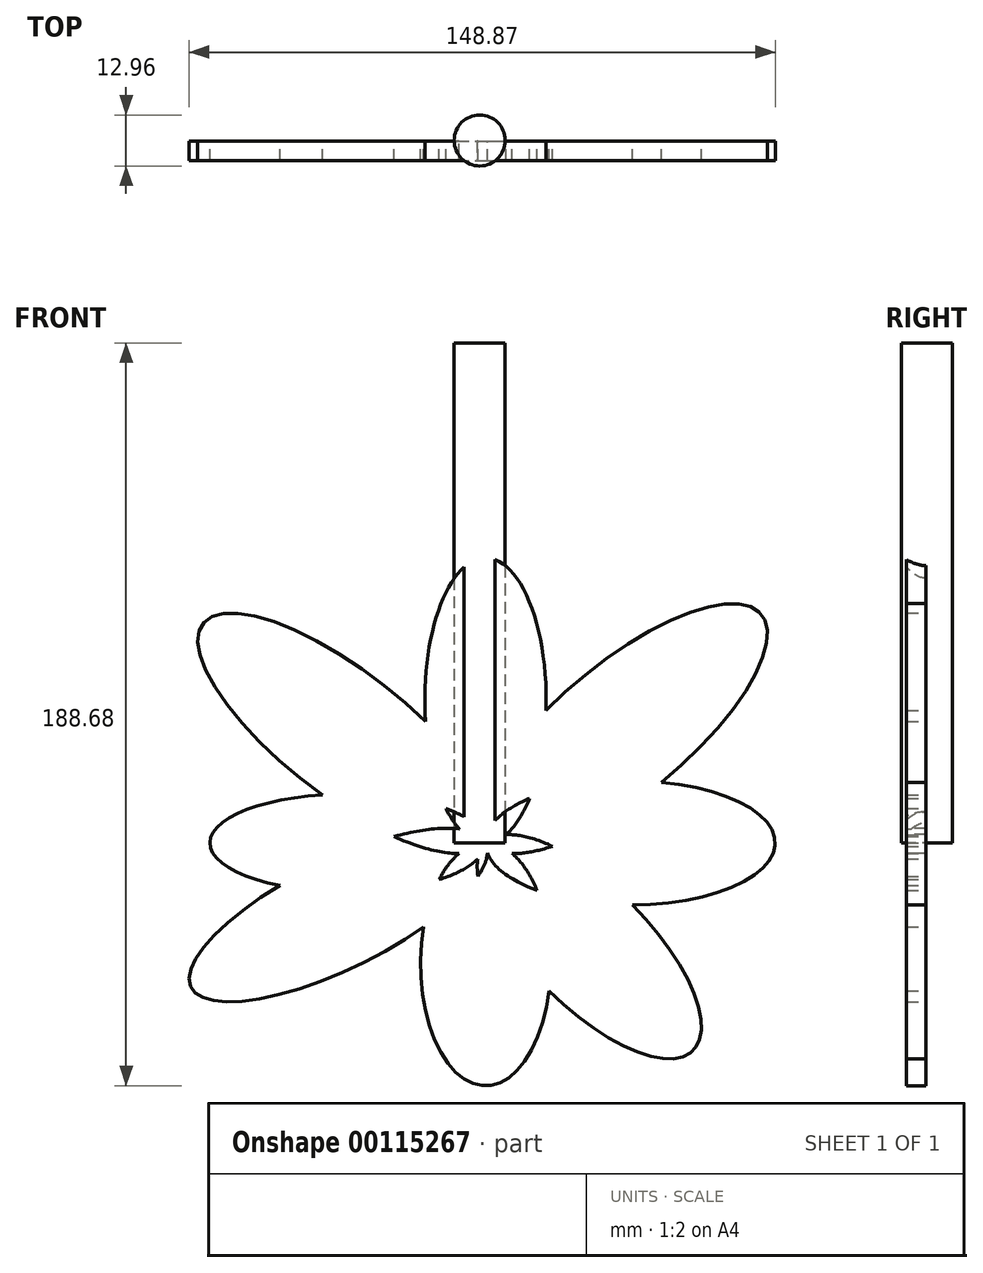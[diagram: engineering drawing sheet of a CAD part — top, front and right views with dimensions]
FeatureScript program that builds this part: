
annotation { "Feature Type Name" : "Feature", "Feature Type Description" : "" }
export const myFeature = defineFeature(function(context is Context, id is Id, definition is map)
    precondition{}
    {
        {
            var Q0;
            Q0=qCreatedBy(makeId("Front.planeOp"),FACE);
            var sketch = newSketch(context, id + "F0", { "sketchPlane" : qUnion([Q0])});
            skEllipse(sketch, "E0", {"center": v(-35.9, 27.86) * mm, "majorRadius": 45.45 * mm, "minorRadius": 15.85 * mm, "majorAxis": v(0.8, -0.61)});
            skEllipse(sketch, "E1", {"center": v(0, 36.2) * mm, "majorRadius": 36.2 * mm, "minorRadius": 15.42 * mm, "majorAxis": v(0, -1)});
            skEllipse(sketch, "E2", {"center": v(35.01, 29.05) * mm, "majorRadius": 45.5 * mm, "minorRadius": 16.7 * mm, "majorAxis": v(-0.77, -0.64)});
            skEllipse(sketch, "E3", {"center": v(36.8, 0) * mm, "majorRadius": 36.8 * mm, "minorRadius": 15.76 * mm, "majorAxis": v(-1, 0)});
            skEllipse(sketch, "E4", {"center": v(0, -30.84) * mm, "majorRadius": 30.84 * mm, "minorRadius": 16.5 * mm, "majorAxis": v(0, 1)});
            skEllipse(sketch, "E5", {"center": v(26.37, -26.37) * mm, "majorRadius": 37.3 * mm, "minorRadius": 15.22 * mm, "majorAxis": v(-0.7, 0.7)});
            skEllipse(sketch, "E6", {"center": v(-37.4, -18.33) * mm, "majorRadius": 41.65 * mm, "minorRadius": 13.65 * mm, "majorAxis": v(0.9, 0.44)});
            skEllipse(sketch, "E7", {"center": v(-35.01, 0) * mm, "majorRadius": 35.01 * mm, "minorRadius": 12.43 * mm, "majorAxis": v(1, 0)});
            skSolve(sketch);
        }
        {
            var Q0;
            Q0 = qSketchRegion(id + "F0", true);
            extrude(context, id + "F1", {"entities" : qUnion([Q0]), "depth" : 5 * mm});
        }
        {
            var Q0;
            Q0=qCreatedBy(makeId("Top.planeOp"),FACE);
            var sketch = newSketch(context, id + "F2", { "sketchPlane" : qUnion([Q0])});
            skCircle(sketch, "E8", {"center": v(-1.47, 0.15) * mm, "radius": 6.48 * mm});
            skSolve(sketch);
        }
        {
            var Q0;
            Q0=makeQuery(id+"F2.imprint","IMPRINT",FACE,{"disambiguationData":[TD([[makeQuery(id+"F2.imprint","IMPRINT",EDGE,{"derivedFrom":sQuery(id+"F2.wireOp",EDGE,"E8")}),1.0]])]});
            extrude(context, id + "F3", {"entities" : qUnion([Q0]), "operationType" : NewBodyOperationType.ADD, "depth" : 127 * mm});
        }
    });
